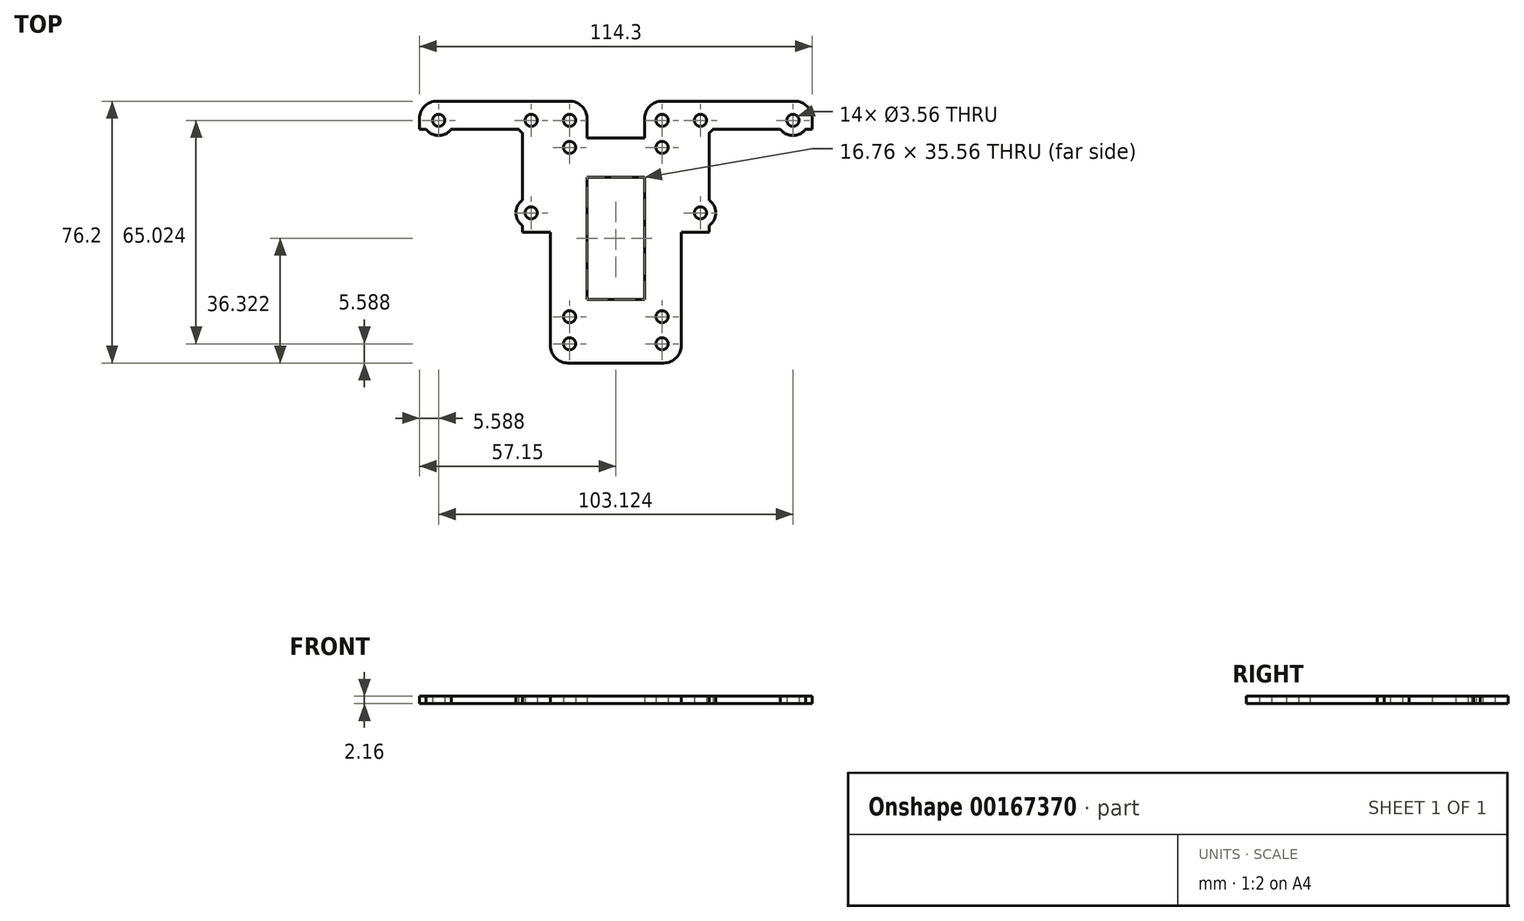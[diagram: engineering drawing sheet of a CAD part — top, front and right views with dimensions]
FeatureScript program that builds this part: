
annotation { "Feature Type Name" : "Feature", "Feature Type Description" : "" }
export const myFeature = defineFeature(function(context is Context, id is Id, definition is map)
    precondition{}
    {
        {
            var Q0;
            Q0=qCreatedBy(makeId("Top.planeOp"),FACE);
            var sketch = newSketch(context, id + "F0", { "sketchPlane" : qUnion([Q0])});
            skPoint(sketch, "E0.middle", {"position": v(0, 0) * mm});
            skCircle(sketch, "E1", {"center": v(13.46, 13.46) * mm, "radius": 1.78 * mm});
            skCircle(sketch, "E2", {"center": v(13.46, 5.59) * mm, "radius": 1.78 * mm});
            skCircle(sketch, "E3", {"center": v(24.64, 13.46) * mm, "radius": 1.78 * mm});
            skCircle(sketch, "E4", {"center": v(51.56, 13.46) * mm, "radius": 1.78 * mm});
            skCircle(sketch, "E5", {"center": v(24.64, -13.46) * mm, "radius": 1.78 * mm});
            skCircle(sketch, "E6", {"center": v(13.46, -51.56) * mm, "radius": 1.78 * mm});
            skCircle(sketch, "E7", {"center": v(13.46, -43.69) * mm, "radius": 1.78 * mm});
            skCircle(sketch, "E8.MirrorC", {"center": v(-24.64, 13.46) * mm, "radius": 1.78 * mm});
            skCircle(sketch, "E9.MirrorC", {"center": v(-13.46, -43.69) * mm, "radius": 1.78 * mm});
            skCircle(sketch, "E10.MirrorC", {"center": v(-24.64, -13.46) * mm, "radius": 1.78 * mm});
            skCircle(sketch, "E11.MirrorC", {"center": v(-13.46, 13.46) * mm, "radius": 1.78 * mm});
            skCircle(sketch, "E12.MirrorC", {"center": v(-13.46, 5.59) * mm, "radius": 1.78 * mm});
            skCircle(sketch, "E13.MirrorC", {"center": v(-51.56, 13.46) * mm, "radius": 1.78 * mm});
            skCircle(sketch, "E14.MirrorC", {"center": v(-13.46, -51.56) * mm, "radius": 1.78 * mm});
            skLineSegment(sketch, "E15.bottom", {"start": v(57.15, 19.05) * mm, "end": v(8.38, 19.05) * mm});
            skLineSegment(sketch, "E15.top", {"start": v(27.18, -19.05) * mm, "end": v(19.05, -19.05) * mm});
            skLineSegment(sketch, "E15.left", {"start": v(57.15, 19.05) * mm, "end": v(57.15, 10.92) * mm});
            skLineSegment(sketch, "E15.right", {"start": v(-57.15, 19.05) * mm, "end": v(-57.15, 10.92) * mm});
            skLineSegment(sketch, "E16.bottom", {"start": v(19.05, -57.15) * mm, "end": v(-19.05, -57.15) * mm});
            skLineSegment(sketch, "E16.left", {"start": v(19.05, -57.15) * mm, "end": v(19.05, -19.05) * mm});
            skLineSegment(sketch, "E16.right", {"start": v(-19.05, -57.15) * mm, "end": v(-19.05, -19.05) * mm});
            skLineSegment(sketch, "E17", {"start": v(-8.38, 19.05) * mm, "end": v(-8.38, 8.38) * mm});
            skLineSegment(sketch, "E18", {"start": v(-8.38, 8.38) * mm, "end": v(8.38, 8.38) * mm});
            skLineSegment(sketch, "E19", {"start": v(8.38, 8.38) * mm, "end": v(8.38, 19.05) * mm});
            skLineSegment(sketch, "E20", {"start": v(-8.38, -3.05) * mm, "end": v(-8.38, -38.6) * mm});
            skLineSegment(sketch, "E21", {"start": v(8.38, -3.05) * mm, "end": v(8.38, -38.6) * mm});
            skLineSegment(sketch, "E22", {"start": v(-8.38, -3.05) * mm, "end": v(8.38, -3.05) * mm});
            skLineSegment(sketch, "E23", {"start": v(-8.38, -38.6) * mm, "end": v(8.38, -38.6) * mm});
            skLineSegment(sketch, "E24.trimOffspring", {"start": v(-19.05, -19.05) * mm, "end": v(-27.18, -19.05) * mm});
            skLineSegment(sketch, "E25", {"start": v(-57.15, 10.92) * mm, "end": v(-55.2, 10.92) * mm});
            skLineSegment(sketch, "E26", {"start": v(-27.18, 9.81) * mm, "end": v(-27.18, -9.81) * mm});
            skLineSegment(sketch, "E27", {"start": v(27.18, -19.05) * mm, "end": v(27.18, -17.1) * mm});
            skLineSegment(sketch, "E28", {"start": v(28.29, 10.92) * mm, "end": v(47.91, 10.92) * mm});
            skLineSegment(sketch, "E29.trimOffspring", {"start": v(-8.38, 19.05) * mm, "end": v(-57.15, 19.05) * mm});
            skCircle(sketch, "E30", {"center": v(51.56, 13.46) * mm, "radius": 4.45 * mm});
            skCircle(sketch, "E31", {"center": v(24.64, 13.46) * mm, "radius": 4.45 * mm});
            skCircle(sketch, "E32", {"center": v(24.64, -13.46) * mm, "radius": 4.45 * mm});
            skLineSegment(sketch, "E33.trimOffspring", {"start": v(55.2, 10.92) * mm, "end": v(57.15, 10.92) * mm});
            skLineSegment(sketch, "E34.trimOffspring", {"start": v(27.18, -9.81) * mm, "end": v(27.18, 9.81) * mm});
            skCircle(sketch, "E35", {"center": v(-51.56, 13.46) * mm, "radius": 4.45 * mm});
            skCircle(sketch, "E36", {"center": v(-24.64, 13.46) * mm, "radius": 4.45 * mm});
            skCircle(sketch, "E37", {"center": v(-24.64, -13.46) * mm, "radius": 4.45 * mm});
            skLineSegment(sketch, "E38.trimOffspring", {"start": v(-47.91, 10.92) * mm, "end": v(-28.29, 10.92) * mm});
            skLineSegment(sketch, "E39.trimOffspring", {"start": v(-27.18, -17.1) * mm, "end": v(-27.18, -19.05) * mm});
            skSolve(sketch);
        }
        {
            var Q0;
            Q0 = qSketchRegion(id + "F0", true);
            extrude(context, id + "F1", {"entities" : qUnion([Q0]), "depth" : 2.16 * mm});
        }
        {
            var Q0;
            Q0=makeQuery(id+"F1.opExtrude","SWEPT_EDGE",EDGE,{"disambiguationData":[OSD([sQuery(id+"F0.wireOp",EDGE,"E15.bottom"),sQuery(id+"F0.wireOp",EDGE,"E15.left")])]});
            var Q1;
            Q1=makeQuery(id+"F1.opExtrude","SWEPT_EDGE",EDGE,{"disambiguationData":[OSD([sQuery(id+"F0.wireOp",EDGE,"E15.bottom"),sQuery(id+"F0.wireOp",EDGE,"E19")])]});
            var Q2;
            Q2=makeQuery(id+"F1.opExtrude","SWEPT_EDGE",EDGE,{"disambiguationData":[OSD([sQuery(id+"F0.wireOp",EDGE,"E17"),sQuery(id+"F0.wireOp",EDGE,"E29.trimOffspring")])]});
            var Q3;
            Q3=makeQuery(id+"F1.opExtrude","SWEPT_EDGE",EDGE,{"disambiguationData":[OSD([sQuery(id+"F0.wireOp",EDGE,"E16.bottom"),sQuery(id+"F0.wireOp",EDGE,"E16.left")])]});
            var Q4;
            Q4=makeQuery(id+"F1.opExtrude","SWEPT_EDGE",EDGE,{"disambiguationData":[OSD([sQuery(id+"F0.wireOp",EDGE,"E16.bottom"),sQuery(id+"F0.wireOp",EDGE,"E16.right")])]});
            var Q5;
            Q5=makeQuery(id+"F1.opExtrude","SWEPT_EDGE",EDGE,{"disambiguationData":[OSD([sQuery(id+"F0.wireOp",EDGE,"E15.right"),sQuery(id+"F0.wireOp",EDGE,"E29.trimOffspring")])]});
            fillet(context, id + "F2", {"entities" : qUnion([Q0, Q1, Q2, Q3, Q4, Q5]), "radius" : 5.08 * mm, "tangentPropagation" : true, "allowEdgeOverflow" : false});
        }
    });
